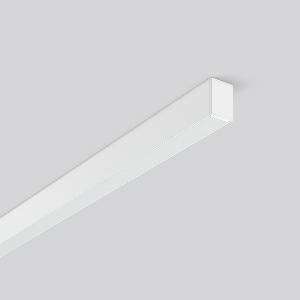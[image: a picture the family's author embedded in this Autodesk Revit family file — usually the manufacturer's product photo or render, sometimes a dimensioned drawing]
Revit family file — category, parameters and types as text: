
# Revit family: less_is_more_27_312201_002_d266
name_source: partatom
category: Lighting Fixtures
units: mm (PartAtom-declared; Revit-internal decimal feet)

## family parameters
Cut with Voids When Loaded = No
Host = Face
Light Source = No
Part Type = Normal
Room Calculation Point = No
Round Connector Dimension = Use Diameter
Shared = No

## types (1)
- LESS IS MORE 27 (1 x LED Modul 830, 3250 lm, 3000)
    Apparent Load = 43 VA
    CIE Flux Codes = 65 89 98 100 100
    Color Rendering = 80
    Color Temperature = 3000
    Default Elevation = 1800 mm
    Description = Series: LESS IS MORE 27
Ceiling luminaire with slim design. Housing: extruded aluminium profile, powder-coated. End cap aluminium powder-coated. Diffuser made of non-yellowing plastic (PMMA) microprismatic. Suitable for Ceiling mounting, Wall (surface). External driver with connecting cable. 
Colour: traffic white, matt (RAL 9016)
Length: 1512 mm
Width: 28 mm
Height: 38 mm
Lamp: LED
Socket: without socket
Colour temperature: 3000K
Colour rendering index (CRI): 82
System power: 43 W
Rated luminous flux: 3250 lm
Luminous efficiency: 76 lm/W
Control gear: Regulated power supply
Protection class: II
Type of protection: IP 20
    Height = 38 mm
    Lamp = 1 x LED Modul 830
    Lamp Light Flux = 3250 lm
    Lamp count = 1
    Length = 1512 mm
    Lifetime = 50000 h
    Luminous efficacy = 76 lm/W
    Manufacturer = RZB
    ModVariant = No
    Model = 312201.002
    Mounting Place = Ceiling, Wall
    Mounting Type = Surface mounted
    Number of Poles = 1
    OnlyDefault = Yes
    Power Factor = 1
    Product Name = LESS IS MORE 27
    Product group = Surface mounted LED linear luminaires
    ProductGroupID = 307
    Protection Class = Protection class II
    Protection Degree = IP 20
    RLX_Detail_Level = 1
    RLX_Emergency_Light_Flux = 0 lm
    RLX_Emergency_Type = 0
    RLX_Emergency_Type_DB = No
    RlxData = <blob elided: 24121 chars, md5=e287aade>
    Socket = socket
    Standby Power = 0 W
    System Light Flux = 3250 lm
    System Power = 43 W
    Type Comments = Product without accessories
    Type Image = 312196.002.jpg
    URL = http://relux.com
    VarID = ---
    Voltage = 230 V
    Voltage Range = 220-240 V
    Weight = 0.00 kg
    Width = 28 mm

## geometry (parser evidence)
native form markers: Blend x4, Sweep x13
no freeform markers — native parametric forms only
